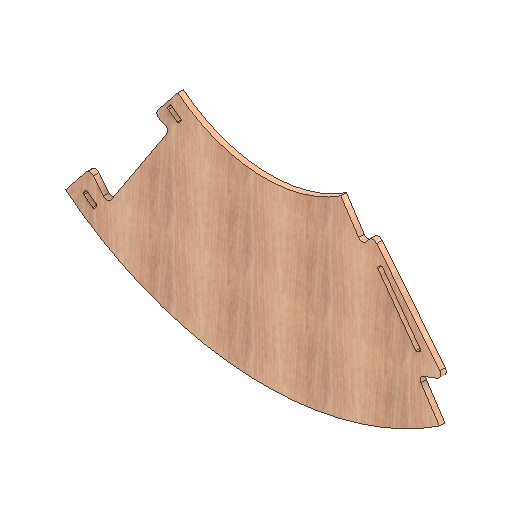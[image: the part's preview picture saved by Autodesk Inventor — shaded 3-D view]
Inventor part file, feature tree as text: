
AUTODESK INVENTOR PART (.ipt)
format: ipt  version: 2021 (Build 250183000, 183)  size: 278,528 bytes
history: native  units: mm
features: other x2, extrude x2, hole x1
ambient origin geometry x8: Origin, YZ Plane, XZ Plane, XY Plane, X Axis, Y Axis, Z Axis, Center Point
bodies: Solid1 (feature_tree)
feature tree (5):
  other  "CONTOURS"
  hole  "HOLES"  [1 undecoded]
  other  "LETTERS"
  extrude  "Extrusion1"  Depth=18.0mm TaperAngle=0.0deg
  extrude  "Extrusion2"  [1 undecoded]
note: 2 required parameter values undecoded (feature->parameter linkage not recoverable at this tier; creation-order binding heuristic only, values carry confidence <= 0.55)
